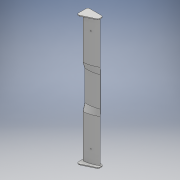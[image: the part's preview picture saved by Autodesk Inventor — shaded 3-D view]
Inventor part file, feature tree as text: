
AUTODESK INVENTOR PART (.ipt)
format: ipt  version: 2018.3 (Build 223284000, 284)  size: 199,168 bytes
history: native  units: mm
features: sketch x6, extrude x4, mirror x2, projected_geometry x2, sweep x1, plane x1
ambient origin geometry x8: Origin, YZ Plane, XZ Plane, XY Plane, X Axis, Y Axis, Z Axis, Center Point
bodies: Solid1 (feature_tree)
feature tree (16):
  extrude  "Extrusion1"  Depth=100.0mm TaperAngle=0.0deg
  sweep  "Sweep1"
  extrude  "Extrusion2"  Depth=4.0mm
  mirror  "Mirror1"
  plane  "Work Plane1"
  extrude  "Extrusion3"  Depth=120.055mm
  mirror  "Mirror2"
  extrude  "Extrusion4"  Depth=3.0mm
  sketch  "Sketch1"  dims[d0=30.0mm d1=100.0mm d2=0.0mm]
  sketch  "Sketch2"  dims[d3=15.0mm d4=0.0mm d5=-1.745329mm]
  projected_geometry  "Projected Loop1"
  sketch  "Sketch3"  dims[d6=35.0mm d7=0.0mm d8=4.0mm]
  sketch  "Sketch4"  dims[d9=2.0mm d10=0.0mm d11=120.055mm]
  projected_geometry  "Projected Loop2"
  sketch  "Sketch5"  dims[d12=120.055mm d13=3.0mm]
  sketch  "Sketch6"  dims[d14=3.0mm d15=20.0mm d16=0.0mm]
